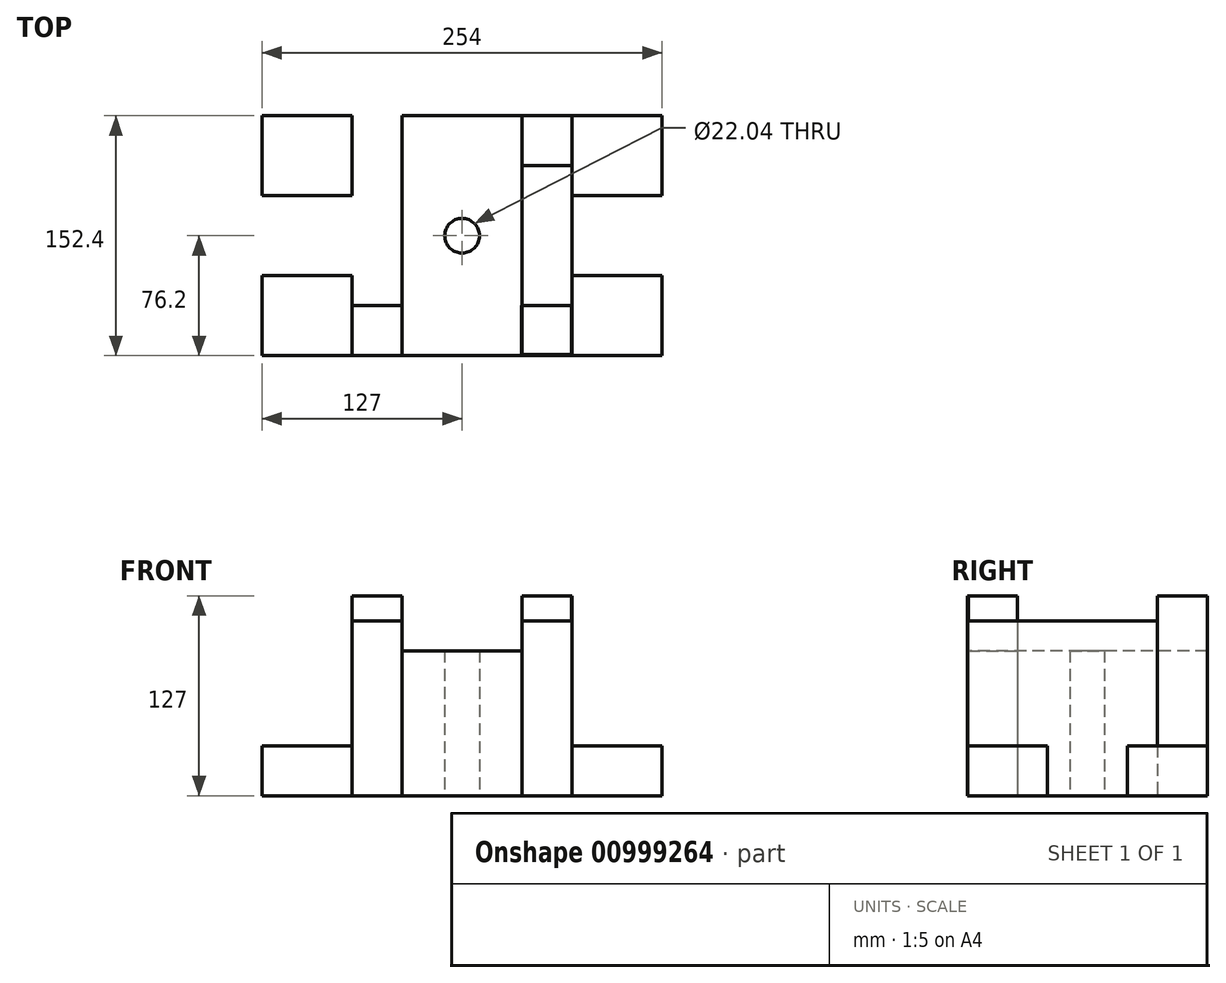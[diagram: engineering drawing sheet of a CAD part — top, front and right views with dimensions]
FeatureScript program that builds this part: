
annotation { "Feature Type Name" : "Feature", "Feature Type Description" : "" }
export const myFeature = defineFeature(function(context is Context, id is Id, definition is map)
    precondition{}
    {
        {
            var Q0;
            Q0=qCreatedBy(makeId("Top.planeOp"),FACE);
            var sketch = newSketch(context, id + "F0", { "sketchPlane" : qUnion([Q0])});
            skLineSegment(sketch, "E0.bottom", {"start": v(-107.95, 76.2) * mm, "end": v(-31.75, 76.2) * mm});
            skLineSegment(sketch, "E0.top", {"start": v(-107.95, -76.2) * mm, "end": v(-31.75, -76.2) * mm});
            skLineSegment(sketch, "E0.left", {"start": v(-107.95, 76.2) * mm, "end": v(-107.95, -76.2) * mm});
            skLineSegment(sketch, "E0.right", {"start": v(-31.75, 76.2) * mm, "end": v(-31.75, -76.2) * mm});
            skLineSegment(sketch, "E1.bottom", {"start": v(-31.75, 76.2) * mm, "end": v(0, 76.2) * mm});
            skLineSegment(sketch, "E1.top", {"start": v(-31.75, -76.2) * mm, "end": v(0, -76.2) * mm});
            skLineSegment(sketch, "E1.right", {"start": v(0, 76.2) * mm, "end": v(0, -76.2) * mm});
            skLineSegment(sketch, "E2.bottom", {"start": v(-107.95, 76.2) * mm, "end": v(-139.7, 76.2) * mm});
            skLineSegment(sketch, "E2.top", {"start": v(-107.95, -76.2) * mm, "end": v(-139.7, -76.2) * mm});
            skLineSegment(sketch, "E2.right", {"start": v(-139.7, 76.2) * mm, "end": v(-139.7, -76.2) * mm});
            skLineSegment(sketch, "E3.bottom", {"start": v(-139.7, 76.2) * mm, "end": v(-107.95, 76.2) * mm});
            skLineSegment(sketch, "E3.left", {"start": v(-139.7, 76.2) * mm, "end": v(-139.7, 64.48) * mm});
            skLineSegment(sketch, "E3.right", {"start": v(-107.95, 76.2) * mm, "end": v(-107.95, 64.56) * mm});
            skLineSegment(sketch, "E4.bottom", {"start": v(-139.7, -76.2) * mm, "end": v(-107.95, -76.2) * mm});
            skLineSegment(sketch, "E4.left", {"start": v(-139.7, -76.2) * mm, "end": v(-139.7, -51.4) * mm});
            skLineSegment(sketch, "E4.right", {"start": v(-107.95, -76.2) * mm, "end": v(-107.95, -51.32) * mm});
            skLineSegment(sketch, "E5.left", {"start": v(-31.75, 76.2) * mm, "end": v(-31.75, 47.94) * mm});
            skLineSegment(sketch, "E5.right", {"start": v(0, 76.2) * mm, "end": v(0, 36.75) * mm});
            skLineSegment(sketch, "E6.left", {"start": v(-31.75, -76.2) * mm, "end": v(-31.75, -50.98) * mm});
            skLineSegment(sketch, "E6.right", {"start": v(0, -76.2) * mm, "end": v(0, -50.9) * mm});
            skLineSegment(sketch, "E7", {"start": v(-139.7, 76.2) * mm, "end": v(-139.7, 44.45) * mm});
            skLineSegment(sketch, "E8.top", {"start": v(-139.7, 44.16) * mm, "end": v(-107.95, 44.16) * mm});
            skLineSegment(sketch, "E8.left", {"start": v(-139.7, 76.2) * mm, "end": v(-139.7, 44.16) * mm});
            skLineSegment(sketch, "E8.right", {"start": v(-107.95, 76.2) * mm, "end": v(-107.95, 44.16) * mm});
            skLineSegment(sketch, "E9", {"start": v(-139.7, -76.2) * mm, "end": v(-139.7, -44.45) * mm});
            skLineSegment(sketch, "E10.bottom", {"start": v(-139.7, -44.45) * mm, "end": v(-107.95, -44.45) * mm});
            skLineSegment(sketch, "E10.left", {"start": v(-139.7, -44.45) * mm, "end": v(-139.7, -76.2) * mm});
            skLineSegment(sketch, "E10.right", {"start": v(-107.95, -44.45) * mm, "end": v(-107.95, -76.2) * mm});
            skLineSegment(sketch, "E11", {"start": v(0, 76.2) * mm, "end": v(0, 44.45) * mm});
            skLineSegment(sketch, "E12.top", {"start": v(-31.75, 44.45) * mm, "end": v(0, 44.45) * mm});
            skLineSegment(sketch, "E12.left", {"start": v(-31.75, 76.2) * mm, "end": v(-31.75, 44.45) * mm});
            skLineSegment(sketch, "E13", {"start": v(0, -76.2) * mm, "end": v(0, -44.45) * mm});
            skLineSegment(sketch, "E14.bottom", {"start": v(-32.06, -75.55) * mm, "end": v(-0.32, -75.55) * mm});
            skLineSegment(sketch, "E14.top", {"start": v(-32.06, -44.37) * mm, "end": v(-0.32, -44.37) * mm});
            skLineSegment(sketch, "E14.left", {"start": v(-32.06, -75.55) * mm, "end": v(-32.06, -44.37) * mm});
            skLineSegment(sketch, "E14.right", {"start": v(-0.32, -75.55) * mm, "end": v(-0.32, -44.37) * mm});
            skCircle(sketch, "E15", {"center": v(-69.85, 0) * mm, "radius": 11.02 * mm});
            skLineSegment(sketch, "E16.bottom", {"start": v(0, 76.2) * mm, "end": v(57.15, 76.2) * mm});
            skLineSegment(sketch, "E16.top", {"start": v(0, 25.4) * mm, "end": v(57.15, 25.4) * mm});
            skLineSegment(sketch, "E16.left", {"start": v(0, 76.2) * mm, "end": v(0, 25.4) * mm});
            skLineSegment(sketch, "E16.right", {"start": v(57.15, 76.2) * mm, "end": v(57.15, 25.4) * mm});
            skLineSegment(sketch, "E17.bottom", {"start": v(0, -76.2) * mm, "end": v(57.15, -76.2) * mm});
            skLineSegment(sketch, "E17.top", {"start": v(0, -25.4) * mm, "end": v(57.15, -25.4) * mm});
            skLineSegment(sketch, "E17.left", {"start": v(0, -76.2) * mm, "end": v(0, -25.4) * mm});
            skLineSegment(sketch, "E17.right", {"start": v(57.15, -76.2) * mm, "end": v(57.15, -25.4) * mm});
            skLineSegment(sketch, "E18.bottom", {"start": v(-139.7, 76.2) * mm, "end": v(-196.85, 76.2) * mm});
            skLineSegment(sketch, "E18.top", {"start": v(-139.7, 25.4) * mm, "end": v(-196.85, 25.4) * mm});
            skLineSegment(sketch, "E18.left", {"start": v(-139.7, 76.2) * mm, "end": v(-139.7, 25.4) * mm});
            skLineSegment(sketch, "E18.right", {"start": v(-196.85, 76.2) * mm, "end": v(-196.85, 25.4) * mm});
            skLineSegment(sketch, "E19.bottom", {"start": v(-139.7, -76.2) * mm, "end": v(-196.85, -76.2) * mm});
            skLineSegment(sketch, "E19.top", {"start": v(-139.7, -25.4) * mm, "end": v(-196.85, -25.4) * mm});
            skLineSegment(sketch, "E19.left", {"start": v(-139.7, -76.2) * mm, "end": v(-139.7, -25.4) * mm});
            skLineSegment(sketch, "E19.right", {"start": v(-196.85, -76.2) * mm, "end": v(-196.85, -25.4) * mm});
            skLineSegment(sketch, "E20", {"start": v(6.35, 25.4) * mm, "end": v(6.35, -25.4) * mm});
            skLineSegment(sketch, "E21", {"start": v(-146.05, 25.4) * mm, "end": v(-146.05, -25.4) * mm});
            skSolve(sketch);
        }
        {
            var Q0;
            Q0=makeQuery(id+"F0.imprint","IMPRINT",FACE,{"disambiguationData":[TD([[makeQuery(id+"F0.imprint","IMPRINT",EDGE,{"derivedFrom":sQuery(id+"F0.wireOp",EDGE,"E3.bottom")}),-1.0]])]});
            var Q1;
            {var subQ1=sQuery(id+"F0.wireOp",EDGE,"E3.bottom");Q1=makeQuery(id+"F0.imprint","IMPRINT",FACE,{"disambiguationData":[TD([[makeQuery(id+"F0.imprint","IMPRINT",EDGE,{"derivedFrom":subQ1}),-1.0]])]});}
            var Q2;
            {var subQ3=sQuery(id+"F0.wireOp",EDGE,"E1.bottom");Q2=makeQuery(id+"F0.imprint","IMPRINT",FACE,{"disambiguationData":[TD([[makeQuery(id+"F0.imprint","IMPRINT",EDGE,{"derivedFrom":subQ3}),-1.0]])]});}
            var Q3;
            {var subQ1=sQuery(id+"F0.wireOp",EDGE,"E10.bottom");Q3=makeQuery(id+"F0.imprint","IMPRINT",FACE,{"disambiguationData":[TD([[makeQuery(id+"F0.imprint","IMPRINT",EDGE,{"derivedFrom":subQ1}),-1.0]])]});}
            var Q4;
            {var subQ0=sQuery(id+"F0.wireOp",EDGE,"E14.right");Q4=makeQuery(id+"F0.imprint","IMPRINT",FACE,{"disambiguationData":[TD([[makeQuery(id+"F0.imprint","IMPRINT",EDGE,{"derivedFrom":subQ0}),1.0]])]});}
            extrude(context, id + "F1", {"entities" : qUnion([Q0, Q1, Q2, Q3, Q4]), "depth" : 127 * mm, "offsetDistance" : 25.4 * mm});
        }
        {
            var Q0;
            Q0=makeQuery(id+"F0.imprint","IMPRINT",FACE,{"disambiguationData":[TD([[makeQuery(id+"F0.imprint","IMPRINT",EDGE,{"derivedFrom":sQuery(id+"F0.wireOp",EDGE,"E0.left")}),-1.0]])]});
            var Q1;
            {var subQ5=sQuery(id+"F0.wireOp",EDGE,"E1.right");Q1=makeQuery(id+"F0.imprint","IMPRINT",FACE,{"disambiguationData":[TD([[makeQuery(id+"F0.imprint","IMPRINT",EDGE,{"derivedFrom":subQ5}),-1.0]])]});}
            extrude(context, id + "F2", {"entities" : qUnion([Q0, Q1]), "depth" : 111.12 * mm, "offsetDistance" : 25.4 * mm});
        }
        {
            var Q0;
            {var subQ5=sQuery(id+"F0.wireOp",EDGE,"E0.bottom");Q0=makeQuery(id+"F0.imprint","IMPRINT",FACE,{"disambiguationData":[TD([[makeQuery(id+"F0.imprint","IMPRINT",EDGE,{"derivedFrom":subQ5}),-1.0]])]});}
            extrude(context, id + "F3", {"entities" : qUnion([Q0]), "depth" : 92.07 * mm, "offsetDistance" : 25.4 * mm});
        }
        {
            var Q0;
            {var subQ3=sQuery(id+"F0.wireOp",EDGE,"E18.bottom");Q0=makeQuery(id+"F0.imprint","IMPRINT",FACE,{"disambiguationData":[TD([[makeQuery(id+"F0.imprint","IMPRINT",EDGE,{"derivedFrom":subQ3}),1.0]])]});}
            var Q1;
            {var subQ3=sQuery(id+"F0.wireOp",EDGE,"E19.bottom");Q1=makeQuery(id+"F0.imprint","IMPRINT",FACE,{"disambiguationData":[TD([[makeQuery(id+"F0.imprint","IMPRINT",EDGE,{"derivedFrom":subQ3}),-1.0]])]});}
            var Q2;
            {var subQ3=sQuery(id+"F0.wireOp",EDGE,"E16.bottom");Q2=makeQuery(id+"F0.imprint","IMPRINT",FACE,{"disambiguationData":[TD([[makeQuery(id+"F0.imprint","IMPRINT",EDGE,{"derivedFrom":subQ3}),-1.0]])]});}
            var Q3;
            {var subQ3=sQuery(id+"F0.wireOp",EDGE,"E17.bottom");Q3=makeQuery(id+"F0.imprint","IMPRINT",FACE,{"disambiguationData":[TD([[makeQuery(id+"F0.imprint","IMPRINT",EDGE,{"derivedFrom":subQ3}),1.0]])]});}
            extrude(context, id + "F4", {"entities" : qUnion([Q0, Q1, Q2, Q3]), "depth" : 31.75 * mm, "offsetDistance" : 25.4 * mm});
        }
        {
            var Q0;
            {var subQ0=sQuery(id+"F0.wireOp",EDGE,"E2.right");Q0=makeQuery(id+"F0.imprint","IMPRINT",FACE,{"disambiguationData":[TD([[makeQuery(id+"F0.imprint","IMPRINT",EDGE,{"derivedFrom":subQ0}),-1.0]])]});}
            var Q1;
            {var subQ0=sQuery(id+"F0.wireOp",EDGE,"E1.right");Q1=makeQuery(id+"F0.imprint","IMPRINT",FACE,{"disambiguationData":[TD([[makeQuery(id+"F0.imprint","IMPRINT",EDGE,{"derivedFrom":subQ0}),1.0]])]});}
            extrude(context, id + "F5", {"entities" : qUnion([Q0, Q1]), "depth" : 31.75 * mm, "offsetDistance" : 25.4 * mm});
        }
    });
